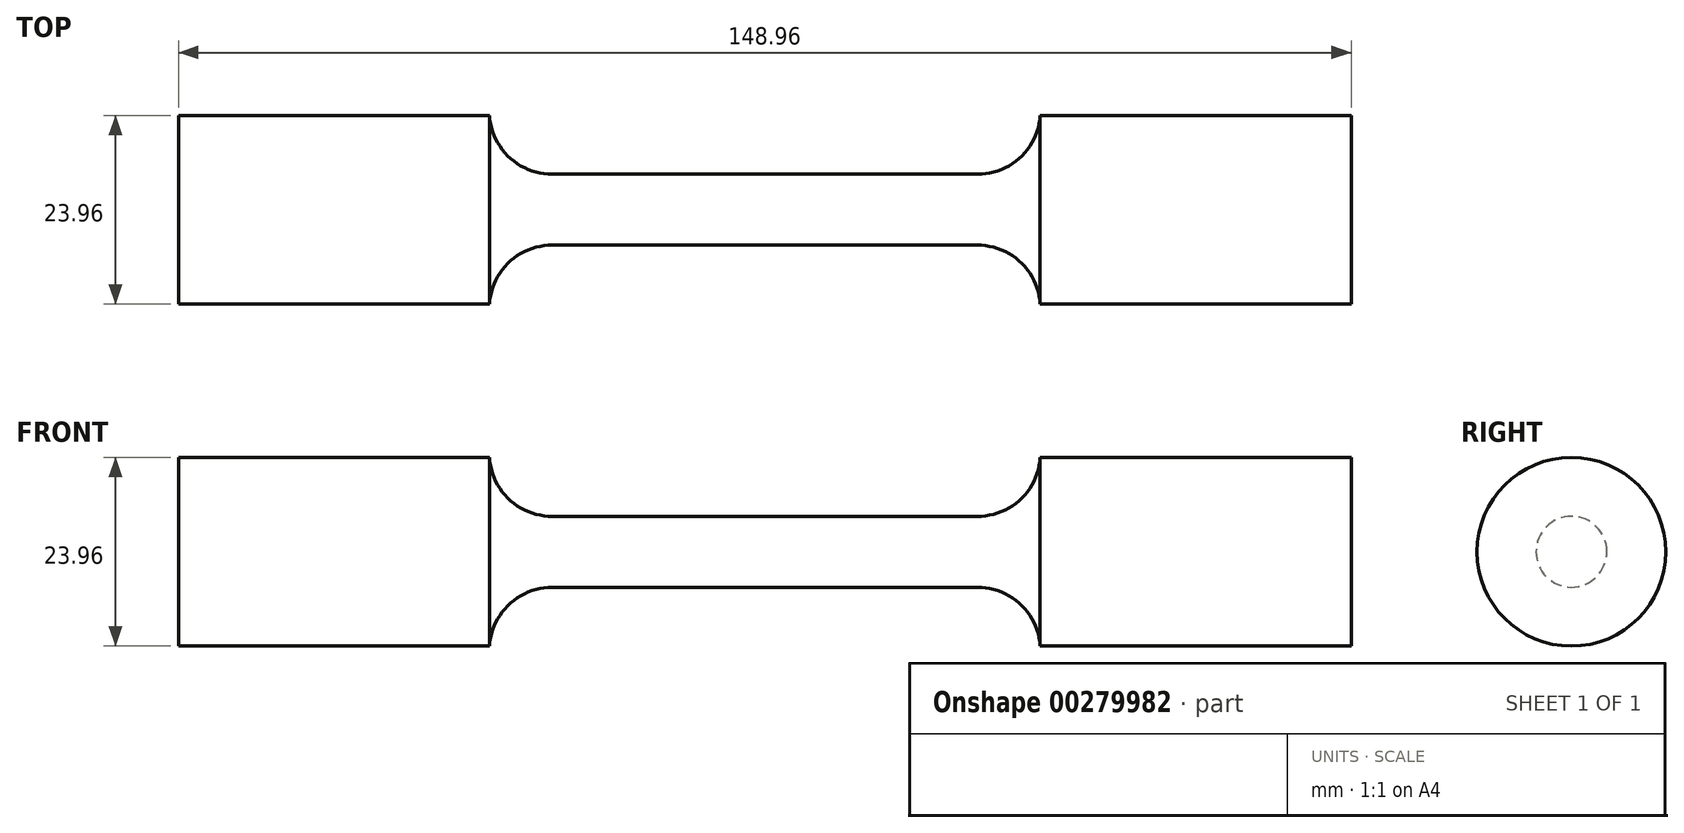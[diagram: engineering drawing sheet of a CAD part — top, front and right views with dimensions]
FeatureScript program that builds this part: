
annotation { "Feature Type Name" : "Feature", "Feature Type Description" : "" }
export const myFeature = defineFeature(function(context is Context, id is Id, definition is map)
    precondition{}
    {
        {
            var Q0;
            Q0=qCreatedBy(makeId("Front.planeOp"),FACE);
            var sketch = newSketch(context, id + "F0", { "sketchPlane" : qUnion([Q0])});
            skLineSegment(sketch, "E0", {"start": v(0, 4.5) * mm, "end": v(27, 4.5) * mm});
            skArc(sketch, "E1", {"start": v(27, 4.5) * mm, "mid": v(32.47, 6.66) * mm, "end": v(34.98, 11.98) * mm});
            skLineSegment(sketch, "E2", {"start": v(34.98, 11.98) * mm, "end": v(74.48, 11.98) * mm});
            skLineSegment(sketch, "E3", {"start": v(74.48, 11.98) * mm, "end": v(74.48, 0) * mm});
            skArc(sketch, "E4.MirrorCS", {"start": v(-27, 4.5) * mm, "mid": v(-32.47, 6.66) * mm, "end": v(-34.98, 11.98) * mm});
            skLineSegment(sketch, "E5.MirrorCS", {"start": v(0, 4.5) * mm, "end": v(-27, 4.5) * mm});
            skLineSegment(sketch, "E6.MirrorCS", {"start": v(-74.48, 11.98) * mm, "end": v(-74.48, 0) * mm});
            skLineSegment(sketch, "E7.MirrorCS", {"start": v(-34.98, 11.98) * mm, "end": v(-74.48, 11.98) * mm});
            skLineSegment(sketch, "E8", {"start": v(-74.48, 0) * mm, "end": v(74.48, 0) * mm});
            skSolve(sketch);
        }
        {
            var Q0;
            Q0 = qSketchRegion(id + "F0", true);
            var Q1;
            Q1=sQuery(id+"F0.wireOp",EDGE,"E8");
            revolve(context, id + "F1", {"entities" : qUnion([Q0]), "axis" : qUnion([Q1]), "revolveType" : RevolveType.FULL});
        }
    });
